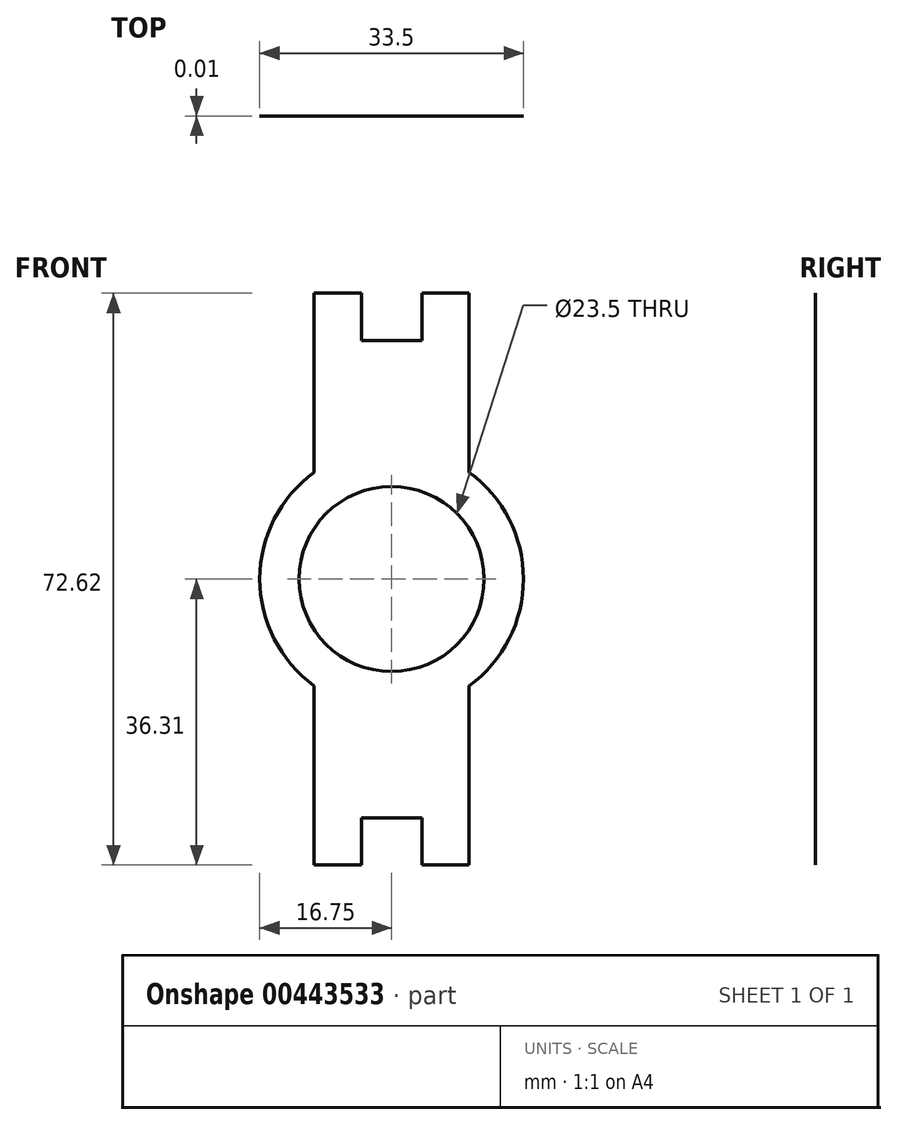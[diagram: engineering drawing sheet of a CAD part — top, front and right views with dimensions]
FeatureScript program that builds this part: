
annotation { "Feature Type Name" : "Feature", "Feature Type Description" : "" }
export const myFeature = defineFeature(function(context is Context, id is Id, definition is map)
    precondition{}
    {
        {
            var Q0;
            Q0=qCreatedBy(makeId("Front.planeOp"),FACE);
            var sketch = newSketch(context, id + "F0", { "sketchPlane" : qUnion([Q0])});
            skCircle(sketch, "E0", {"center": v(0, 0) * mm, "radius": 11.75 * mm});
            skCircle(sketch, "E1", {"center": v(0, 0) * mm, "radius": 16.75 * mm});
            skLineSegment(sketch, "E2.bottom", {"start": v(-9.85, -30.31) * mm, "end": v(9.85, -30.31) * mm});
            skLineSegment(sketch, "E2.top", {"start": v(-9.85, 30.31) * mm, "end": v(9.85, 30.31) * mm});
            skLineSegment(sketch, "E2.left", {"start": v(-9.85, -30.31) * mm, "end": v(-9.85, 30.31) * mm});
            skLineSegment(sketch, "E2.right", {"start": v(9.85, -30.31) * mm, "end": v(9.85, 30.31) * mm});
            skPoint(sketch, "E3", {"position": v(-9.85, 0) * mm});
            skPoint(sketch, "E4", {"position": v(9.85, 0) * mm});
            skPoint(sketch, "E5", {"position": v(-9.85, 6.4) * mm});
            skPoint(sketch, "E6", {"position": v(-9.85, -6.4) * mm});
            skPoint(sketch, "E7", {"position": v(9.85, -6.4) * mm});
            skPoint(sketch, "E8", {"position": v(9.85, 6.4) * mm});
            skSolve(sketch);
        }
        {
            var Q0;
            Q0 = qSketchRegion(id + "F0", true);
            extrude(context, id + "F1", {"entities" : qUnion([Q0]), "depth" : 1 / 101.6 * mm});
        }
        {
            var Q0;
            Q0=makeQuery(id+"F1.opExtrude","CAP_FACE",FACE,{"disambiguationData":[OSD([sQuery(id+"F0.wireOp",EDGE,"E0"),sQuery(id+"F0.wireOp",EDGE,"E1"),sQuery(id+"F0.wireOp",EDGE,"E2.bottom"),sQuery(id+"F0.wireOp",EDGE,"E2.top"),sQuery(id+"F0.wireOp",EDGE,"E2.left"),sQuery(id+"F0.wireOp",EDGE,"E2.right")])],"isStart":false});
            var sketch = newSketch(context, id + "F2", { "sketchPlane" : qUnion([Q0])});
            skLineSegment(sketch, "E9.bottom", {"start": v(-9.85, 30.31) * mm, "end": v(-3.85, 30.31) * mm});
            skLineSegment(sketch, "E9.top", {"start": v(-9.85, 36.31) * mm, "end": v(-3.85, 36.31) * mm});
            skLineSegment(sketch, "E9.left", {"start": v(-9.85, 30.31) * mm, "end": v(-9.85, 36.31) * mm});
            skLineSegment(sketch, "E9.right", {"start": v(-3.85, 30.31) * mm, "end": v(-3.85, 36.31) * mm});
            skLineSegment(sketch, "E10.bottom", {"start": v(9.85, 30.31) * mm, "end": v(3.85, 30.31) * mm});
            skLineSegment(sketch, "E10.top", {"start": v(9.85, 36.31) * mm, "end": v(3.85, 36.31) * mm});
            skLineSegment(sketch, "E10.left", {"start": v(9.85, 30.31) * mm, "end": v(9.85, 36.31) * mm});
            skLineSegment(sketch, "E10.right", {"start": v(3.85, 30.31) * mm, "end": v(3.85, 36.31) * mm});
            skLineSegment(sketch, "E11.bottom", {"start": v(-9.85, -30.31) * mm, "end": v(-3.85, -30.31) * mm});
            skLineSegment(sketch, "E11.top", {"start": v(-9.85, -36.31) * mm, "end": v(-3.85, -36.31) * mm});
            skLineSegment(sketch, "E11.left", {"start": v(-9.85, -30.31) * mm, "end": v(-9.85, -36.31) * mm});
            skLineSegment(sketch, "E11.right", {"start": v(-3.85, -30.31) * mm, "end": v(-3.85, -36.31) * mm});
            skLineSegment(sketch, "E12.bottom", {"start": v(9.85, -30.31) * mm, "end": v(3.85, -30.31) * mm});
            skLineSegment(sketch, "E12.top", {"start": v(9.85, -36.31) * mm, "end": v(3.85, -36.31) * mm});
            skLineSegment(sketch, "E12.left", {"start": v(9.85, -30.31) * mm, "end": v(9.85, -36.31) * mm});
            skLineSegment(sketch, "E12.right", {"start": v(3.85, -30.31) * mm, "end": v(3.85, -36.31) * mm});
            skSolve(sketch);
        }
        {
            var Q0;
            Q0 = qSketchRegion(id + "F2", true);
            extrude(context, id + "F3", {"entities" : qUnion([Q0]), "operationType" : NewBodyOperationType.ADD, "oppositeDirection" : true, "depth" : 1 / 101.6 * mm});
        }
    });
